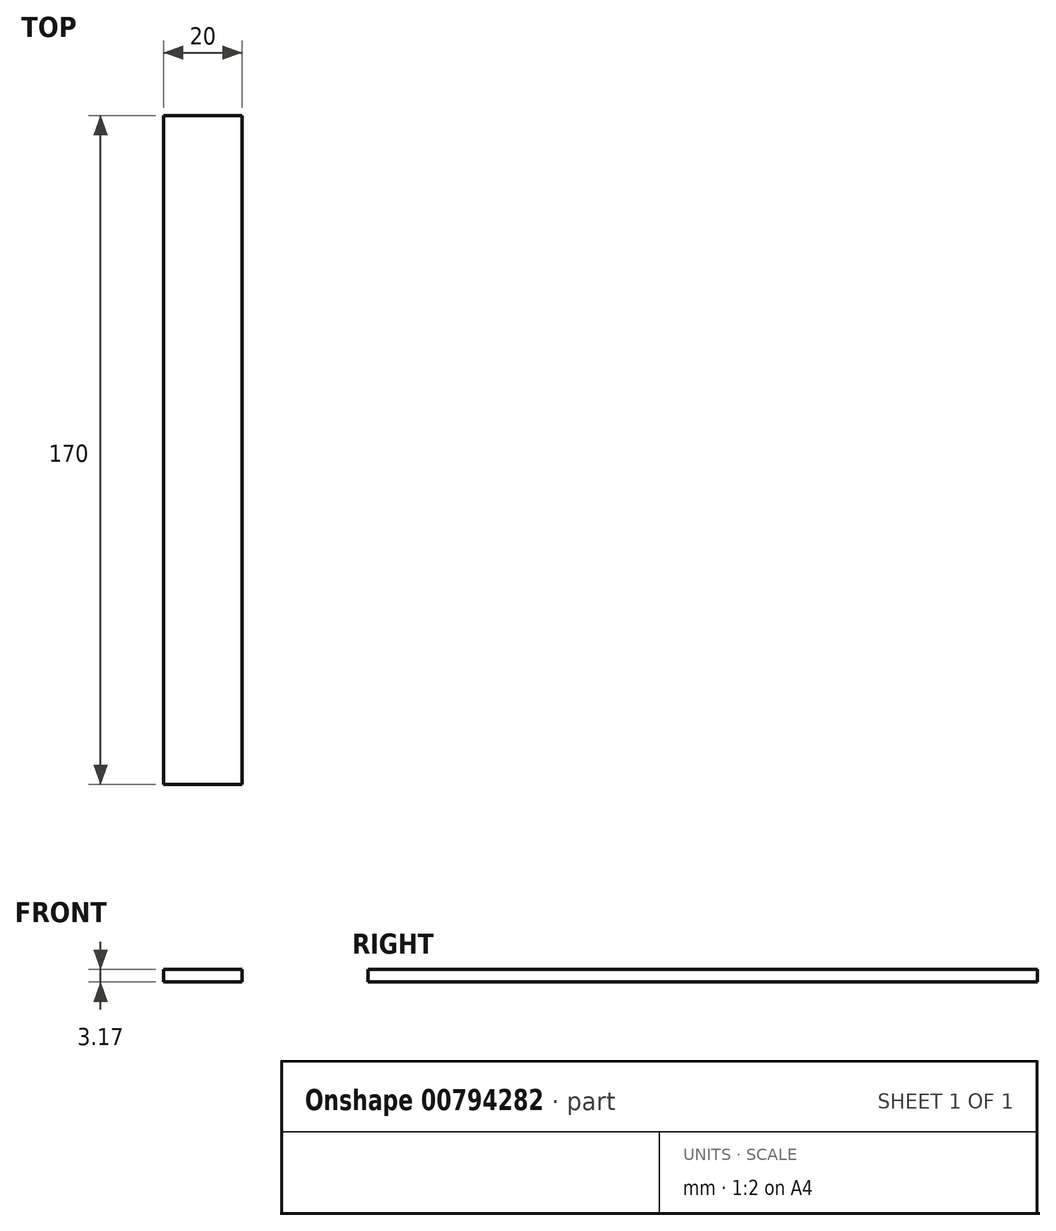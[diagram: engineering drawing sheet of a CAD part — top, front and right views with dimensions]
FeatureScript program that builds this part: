
annotation { "Feature Type Name" : "Feature", "Feature Type Description" : "" }
export const myFeature = defineFeature(function(context is Context, id is Id, definition is map)
    precondition{}
    {
        {
            var Q0;
            Q0=qCreatedBy(makeId("Top.planeOp"),FACE);
            var sketch = newSketch(context, id + "F0", { "sketchPlane" : qUnion([Q0])});
            skLineSegment(sketch, "E0.bottom", {"start": v(-9.89, 80.4) * mm, "end": v(10.11, 80.4) * mm});
            skLineSegment(sketch, "E0.top", {"start": v(-9.89, -89.6) * mm, "end": v(10.11, -89.6) * mm});
            skLineSegment(sketch, "E0.left", {"start": v(-9.89, 80.4) * mm, "end": v(-9.89, -89.6) * mm});
            skLineSegment(sketch, "E0.right", {"start": v(10.11, 80.4) * mm, "end": v(10.11, -89.6) * mm});
            skSolve(sketch);
        }
        {
            var Q0;
            Q0=makeQuery(id+"F0.imprint","IMPRINT",FACE,{"disambiguationData":[TD([[makeQuery(id+"F0.imprint","IMPRINT",EDGE,{"derivedFrom":sQuery(id+"F0.wireOp",EDGE,"E0.bottom")}),-1.0]])]});
            extrude(context, id + "F1", {"entities" : qUnion([Q0]), "depth" : 3.17 * mm, "offsetDistance" : 25.4 * mm});
        }
    });
